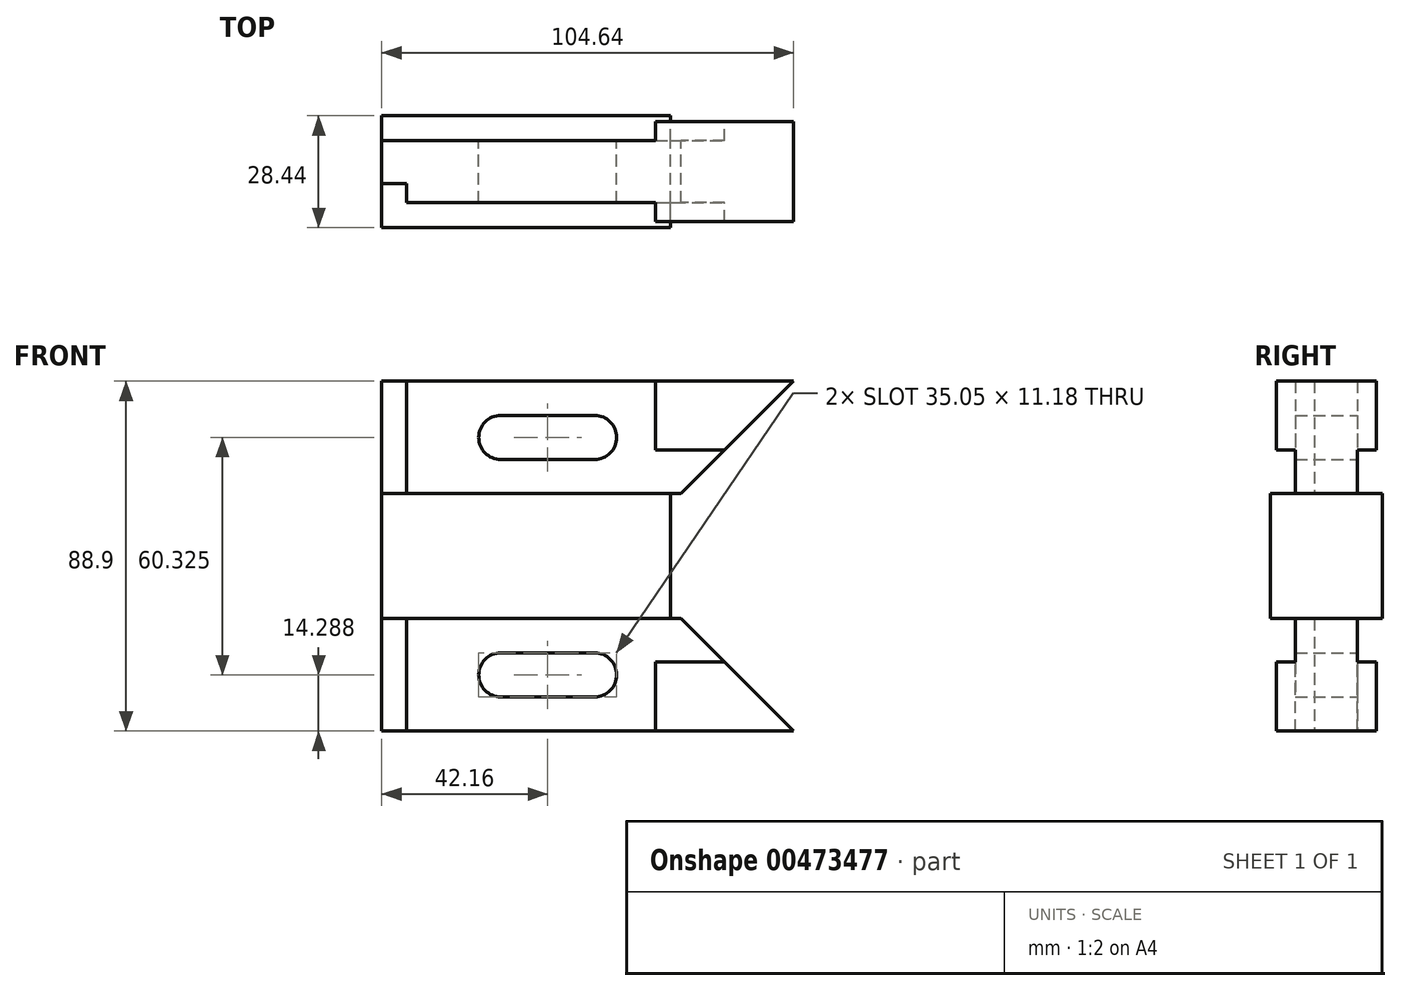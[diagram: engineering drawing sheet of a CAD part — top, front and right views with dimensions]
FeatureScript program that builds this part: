
annotation { "Feature Type Name" : "Feature", "Feature Type Description" : "" }
export const myFeature = defineFeature(function(context is Context, id is Id, definition is map)
    precondition{}
    {
        {
            var Q0;
            Q0=qCreatedBy(makeId("Front.planeOp"),FACE);
            var sketch = newSketch(context, id + "F0", { "sketchPlane" : qUnion([Q0])});
            skLineSegment(sketch, "E0.bottom", {"start": v(-52.32, 44.45) * mm, "end": v(52.32, 44.45) * mm});
            skLineSegment(sketch, "E0.top", {"start": v(-52.32, -44.45) * mm, "end": v(52.32, -44.45) * mm});
            skLineSegment(sketch, "E0.left", {"start": v(-52.32, 44.45) * mm, "end": v(-52.32, -44.45) * mm});
            skPoint(sketch, "E0.middle", {"position": v(0, 0) * mm});
            skLineSegment(sketch, "E1", {"start": v(-52.32, 15.87) * mm, "end": v(21.08, 15.87) * mm});
            skLineSegment(sketch, "E2.MirrorCS", {"start": v(-52.32, -15.87) * mm, "end": v(21.08, -15.87) * mm});
            skLineSegment(sketch, "E3", {"start": v(21.08, 15.87) * mm, "end": v(21.08, -15.87) * mm});
            skLineSegment(sketch, "E4", {"start": v(52.32, 44.45) * mm, "end": v(23.75, 15.87) * mm});
            skLineSegment(sketch, "E5", {"start": v(21.08, 15.87) * mm, "end": v(23.75, 15.87) * mm});
            skLineSegment(sketch, "E6.MirrorCS", {"start": v(52.32, -44.45) * mm, "end": v(23.75, -15.87) * mm});
            skLineSegment(sketch, "E7", {"start": v(21.08, -15.87) * mm, "end": v(23.75, -15.87) * mm});
            skLineSegment(sketch, "E8", {"start": v(17.27, 44.45) * mm, "end": v(17.27, 26.92) * mm});
            skLineSegment(sketch, "E9", {"start": v(17.27, 26.92) * mm, "end": v(34.8, 26.92) * mm});
            skLineSegment(sketch, "E10.MirrorCS", {"start": v(17.27, -44.45) * mm, "end": v(17.27, -26.92) * mm});
            skLineSegment(sketch, "E11.MirrorCS", {"start": v(17.27, -26.92) * mm, "end": v(34.8, -26.92) * mm});
            skLineSegment(sketch, "E12", {"start": v(-45.97, 44.45) * mm, "end": v(-45.97, 15.88) * mm});
            skLineSegment(sketch, "E13.MirrorCS", {"start": v(-45.97, -44.45) * mm, "end": v(-45.97, -15.88) * mm});
            skPoint(sketch, "E14.startSnap0", {"position": v(-45.97, -30.16) * mm});
            skArc(sketch, "E15", {"start": v(-22.1, -24.57) * mm, "mid": v(-27.69, -30.16) * mm, "end": v(-22.1, -35.75) * mm});
            skLineSegment(sketch, "E16", {"start": v(-22.1, -24.57) * mm, "end": v(1.78, -24.57) * mm});
            skLineSegment(sketch, "E17", {"start": v(-22.1, -35.75) * mm, "end": v(1.78, -35.75) * mm});
            skArc(sketch, "E18", {"start": v(1.78, -35.75) * mm, "mid": v(7.37, -30.16) * mm, "end": v(1.78, -24.57) * mm});
            skArc(sketch, "E19.MirrorCS", {"start": v(-22.1, 24.57) * mm, "mid": v(-27.69, 30.16) * mm, "end": v(-22.1, 35.75) * mm});
            skLineSegment(sketch, "E20.MirrorCS", {"start": v(-22.1, 24.57) * mm, "end": v(1.78, 24.57) * mm});
            skLineSegment(sketch, "E21.MirrorCS", {"start": v(-22.1, 35.75) * mm, "end": v(1.78, 35.75) * mm});
            skArc(sketch, "E22.MirrorCS", {"start": v(1.78, 35.75) * mm, "mid": v(7.37, 30.16) * mm, "end": v(1.78, 24.57) * mm});
            skSolve(sketch);
        }
        {
            var Q0;
            {var subQ4=sQuery(id+"F0.wireOp",EDGE,"E3");Q0=makeQuery(id+"F0.imprint","IMPRINT",FACE,{"disambiguationData":[TD([[makeQuery(id+"F0.imprint","IMPRINT",EDGE,{"derivedFrom":subQ4}),-1.0]])]});}
            extrude(context, id + "F1", {"entities" : qUnion([Q0]), "endBound" : BoundingType.SYMMETRIC, "depth" : 28.45 * mm});
        }
        {
            var Q0;
            {var subQ3=sQuery(id+"F0.wireOp",EDGE,"E5");Q0=makeQuery(id+"F0.imprint","IMPRINT",FACE,{"disambiguationData":[TD([[makeQuery(id+"F0.imprint","IMPRINT",EDGE,{"derivedFrom":subQ3}),1.0]])]});}
            var Q1;
            {var subQ3=sQuery(id+"F0.wireOp",EDGE,"E7");Q1=makeQuery(id+"F0.imprint","IMPRINT",FACE,{"disambiguationData":[TD([[makeQuery(id+"F0.imprint","IMPRINT",EDGE,{"derivedFrom":subQ3}),-1.0]])]});}
            extrude(context, id + "F2", {"entities" : qUnion([Q0, Q1]), "operationType" : NewBodyOperationType.ADD, "endBound" : BoundingType.SYMMETRIC, "depth" : 15.75 * mm});
        }
        {
            var Q0;
            {var subQ3=sQuery(id+"F0.wireOp",EDGE,"E8");Q0=makeQuery(id+"F0.imprint","IMPRINT",FACE,{"disambiguationData":[TD([[makeQuery(id+"F0.imprint","IMPRINT",EDGE,{"derivedFrom":subQ3}),1.0]])]});}
            var Q1;
            {var subQ3=sQuery(id+"F0.wireOp",EDGE,"E10.MirrorCS");Q1=makeQuery(id+"F0.imprint","IMPRINT",FACE,{"disambiguationData":[TD([[makeQuery(id+"F0.imprint","IMPRINT",EDGE,{"derivedFrom":subQ3}),-1.0]])]});}
            extrude(context, id + "F3", {"entities" : qUnion([Q0, Q1]), "operationType" : NewBodyOperationType.ADD, "endBound" : BoundingType.SYMMETRIC, "depth" : 25.4 * mm});
        }
        {
            var Q0;
            {var subQ3=sQuery(id+"F0.wireOp",EDGE,"E12");Q0=makeQuery(id+"F0.imprint","IMPRINT",FACE,{"disambiguationData":[TD([[makeQuery(id+"F0.imprint","IMPRINT",EDGE,{"derivedFrom":subQ3}),-1.0]])]});}
            var Q1;
            {var subQ3=sQuery(id+"F0.wireOp",EDGE,"E13.MirrorCS");Q1=makeQuery(id+"F0.imprint","IMPRINT",FACE,{"disambiguationData":[TD([[makeQuery(id+"F0.imprint","IMPRINT",EDGE,{"derivedFrom":subQ3}),1.0]])]});}
            extrude(context, id + "F4", {"entities" : qUnion([Q0, Q1]), "operationType" : NewBodyOperationType.ADD, "endBound" : BoundingType.SYMMETRIC, "depth" : 25.4 * mm});
        }
        {
            var Q0;
            Q0=makeQuery(id+"F4.opExtrude","CAP_FACE",FACE,{"disambiguationData":[OSD([sQuery(id+"F0.wireOp",EDGE,"E0.bottom"),sQuery(id+"F0.wireOp",EDGE,"E0.left"),sQuery(id+"F0.wireOp",EDGE,"E1"),sQuery(id+"F0.wireOp",EDGE,"E12")])],"isStart":false});
            var Q1;
            Q1=makeQuery(id+"F4.opExtrude","CAP_FACE",FACE,{"disambiguationData":[OSD([sQuery(id+"F0.wireOp",EDGE,"E0.top"),sQuery(id+"F0.wireOp",EDGE,"E0.left"),sQuery(id+"F0.wireOp",EDGE,"E2.MirrorCS"),sQuery(id+"F0.wireOp",EDGE,"E13.MirrorCS")])],"isStart":false});
            extrude(context, id + "F5", {"entities" : qUnion([Q0, Q1]), "operationType" : NewBodyOperationType.REMOVE, "oppositeDirection" : true, "depth" : 9.65 * mm});
        }
        {
            var Q0;
            Q0=makeQuery(id+"F4.opExtrude","CAP_FACE",FACE,{"disambiguationData":[OSD([sQuery(id+"F0.wireOp",EDGE,"E0.bottom"),sQuery(id+"F0.wireOp",EDGE,"E0.left"),sQuery(id+"F0.wireOp",EDGE,"E1"),sQuery(id+"F0.wireOp",EDGE,"E12")])],"isStart":true});
            var Q1;
            Q1=makeQuery(id+"F4.opExtrude","CAP_FACE",FACE,{"disambiguationData":[OSD([sQuery(id+"F0.wireOp",EDGE,"E0.top"),sQuery(id+"F0.wireOp",EDGE,"E0.left"),sQuery(id+"F0.wireOp",EDGE,"E2.MirrorCS"),sQuery(id+"F0.wireOp",EDGE,"E13.MirrorCS")])],"isStart":true});
            extrude(context, id + "F6", {"entities" : qUnion([Q0, Q1]), "operationType" : NewBodyOperationType.REMOVE, "oppositeDirection" : true, "depth" : 4.83 * mm});
        }
    });
